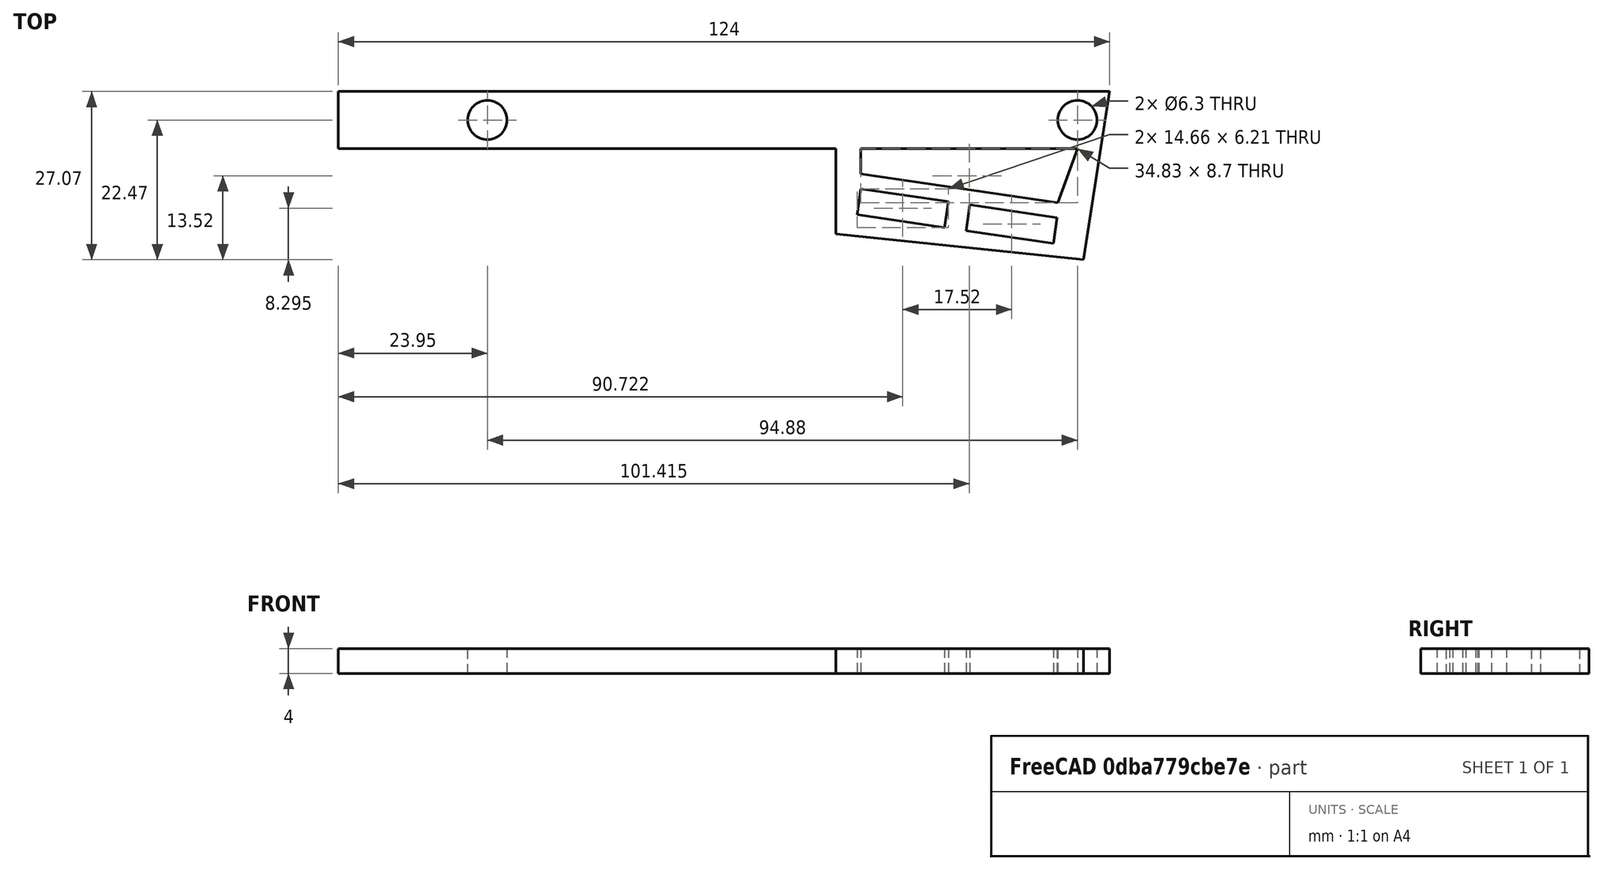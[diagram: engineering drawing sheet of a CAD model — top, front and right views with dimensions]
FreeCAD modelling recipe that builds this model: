
FCSTD DOCUMENT  (FreeCAD 0.18.1R)
Label: CHASSIS
License: All rights reserved
LicenseURL: http://en.wikipedia.org/wiki/All_rights_reserved
objects: TechDraw::DrawViewDimension×12, TechDraw::DrawProjGroupItem×4, Sketcher::SketchObject×2, TechDraw::DrawSVGTemplate×2, TechDraw::DrawPage×2, PartDesign::Pad×1, PartDesign::Plane×1, PartDesign::Pocket×1, PartDesign::Body×1, TechDraw::DrawViewPart×1, TechDraw::DrawProjGroup×1
note: 8 computed .brp shape members not serialized (recipe doc carries the construction recipe); baked Part::Feature solids carry a one-line shape summary decoded from their .brp

FEATURE [Sketcher::SketchObject] Sketch
  MapMode = 5
  Support = -> [XY_Plane]
  sketch-geometry (6):
    g0: LineSegment StartX=0 StartY=9.2 StartZ=0 EndX=0 EndY=0 EndZ=0
    g1: LineSegment StartX=0 StartY=0 StartZ=0 EndX=80 EndY=0 EndZ=0
    g2: LineSegment StartX=80 StartY=0 StartZ=0 EndX=80 EndY=-13.7 EndZ=0
    g3: LineSegment StartX=124 StartY=9.2 StartZ=0 EndX=0 EndY=9.2 EndZ=0
    g4: LineSegment StartX=80 StartY=-13.7 StartZ=0 EndX=119.782 EndY=-17.8733 EndZ=0
    g5: LineSegment StartX=124 StartY=9.2 StartZ=0 EndX=119.782 EndY=-17.8733 EndZ=0
  constraints (17):
    c: Vertical(g0)
    c: Coincident(g0,g1)
    c: Horizontal(g1)
    c: Coincident(g1,g2)
    c: Coincident(g3,g0)
    c: Horizontal(g3)
    c: DistanceX(g3,g3) = 124
    c: DistanceY(g0,g0) = 9.2
    c: DistanceX(g1,g1) = 80
    c: Coincident(g4,g2)
    c: Distance(g4) = 40
    c: Coincident(g5,g3)
    c: Coincident(g5,g4)
    c: Distance(g5) = 27.4
    c: Distance(g2) = 13.7
    c: Vertical(g2)
    c: Coincident(g0,g-1)
FEATURE [PartDesign::Pad] Pad
  Length = 4
  Length2 = 100
  Profile = -> Sketch
  Refine = true
  Type = 0
FEATURE [PartDesign::Plane] DatumPlane
  Length = 146.223
  MapMode = 5
  Placement = pos=(0,0,4) rot=(0,0,1;0rad)
  ResizeMode = 0
  Support = -> [Pad]
  Width = 40.0963
FEATURE [Sketcher::SketchObject] Sketch001
  MapMode = 5
  Placement = pos=(0,0,4) rot=(0,0,1;0rad)
  Support = -> [DatumPlane]
  sketch-geometry (14):
    g0: Circle CenterX=23.95 CenterY=4.6 CenterZ=0 NormalX=0 NormalY=0 NormalZ=1 AngleXU=0 Radius=3.15
    g1: Circle CenterX=118.83 CenterY=4.6 CenterZ=0 NormalX=0 NormalY=0 NormalZ=1 AngleXU=0 Radius=3.15
    g2: LineSegment StartX=84 StartY=0 StartZ=0 EndX=118.83 EndY=0 EndZ=0
    g3: LineSegment StartX=118.83 StartY=0 StartZ=0 EndX=115.67 EndY=-8.7 EndZ=0
    g4: LineSegment StartX=115.67 StartY=-8.7 StartZ=0 EndX=84 EndY=-4.07 EndZ=0
    g5: LineSegment StartX=84 StartY=-4.07 StartZ=0 EndX=84 EndY=0 EndZ=0
    g6: LineSegment StartX=84 StartY=-6.47 StartZ=0 EndX=98.0506 EndY=-8.52414 EndZ=0
    g7: LineSegment StartX=98.0506 StartY=-8.52414 StartZ=0 EndX=97.4431 EndY=-12.68 EndZ=0
    g8: LineSegment StartX=97.4431 StartY=-12.68 StartZ=0 EndX=83.3924 EndY=-10.6258 EndZ=0
    g9: LineSegment StartX=83.3924 StartY=-10.6258 StartZ=0 EndX=84 EndY=-6.47 EndZ=0
    g10: LineSegment StartX=101.52 StartY=-9.03 StartZ=0 EndX=115.571 EndY=-11.0841 EndZ=0
    g11: LineSegment StartX=115.571 StartY=-11.0841 StartZ=0 EndX=114.963 EndY=-15.24 EndZ=0
    g12: LineSegment StartX=114.963 StartY=-15.24 StartZ=0 EndX=100.912 EndY=-13.1858 EndZ=0
    g13: LineSegment StartX=100.912 StartY=-13.1858 StartZ=0 EndX=101.52 EndY=-9.03 EndZ=0
  constraints (42):
    c: Radius(g1) = 3.15
    c: Radius(g0) = 3.15
    c: DistanceX(g-1,g0) = 23.95
    c: DistanceY(g-1,g0) = 4.6
    c: DistanceY(g0,g1) = 0
    c: Horizontal(g2)
    c: Coincident(g2,g3)
    c: Coincident(g3,g4)
    c: Coincident(g4,g5)
    c: Coincident(g5,g2)
    c: DistanceY(g2,g-1) = 0
    c: DistanceX(g-1,g2) = 84
    c: Vertical(g5)
    c: DistanceX(g2,g2) = 34.83
    c: DistanceX(g3,g2) = 3.16
    c: DistanceY(g3,g2) = 8.7
    c: DistanceY(g4,g2) = 4.07
    c: DistanceX(g1,g2) = 0
    c: Coincident(g6,g7)
    c: Coincident(g7,g8)
    c: Coincident(g8,g9)
    c: Coincident(g9,g6)
    c: Coincident(g10,g11)
    c: Coincident(g11,g12)
    c: Coincident(g12,g13)
    c: Coincident(g13,g10)
    c: Parallel(g6,g4)
    c: Parallel(g10,g4)
    c: Distance(g10) = 14.2
    c: Perpendicular(g6,g9)
    c: Perpendicular(g6,g7)
    c: Parallel(g8,g6)
    c: Distance(g7) = 4.2
    c: Perpendicular(g10,g13)
    c: Perpendicular(g10,g11)
    c: Parallel(g12,g10)
    c: Equal(g7,g13)
    c: Equal(g6,g10)
    c: DistanceX(g4,g6) = 0
    c: DistanceY(g6,g4) = 2.4
    c: DistanceY(g10,g4) = 4.96
    c: DistanceX(g4,g10) = 17.52
FEATURE [PartDesign::Pocket] Pocket
  BaseFeature = -> Pad
  Length = 5
  Length2 = 100
  Profile = -> Sketch001
  Refine = true
  Type = 0
FEATURE [PartDesign::Body] Body
  Group = -> [Sketch,Pad,DatumPlane,Sketch001,Pocket]
  Origin = -> Origin
  Tip = -> Pocket
FEATURE [TechDraw::DrawSVGTemplate] Template
  EditableTexts = Designed_by_Name=Designed by Name; Drawing_number=Drawing number; FC-Date=Date; FC-SC=Scale; FC-SH=Sheet; FC-Title=Title; Subtitle=Subtitle; Weight=Weight
  Height = 210
  Orientation = 1
  Width = 297
FEATURE [TechDraw::DrawViewPart] View
  CoarseView = false
  Direction = (0,-1,0)
  Focus = 100
  HardHidden = false
  IsoCount = 0
  IsoHidden = false
  IsoVisible = false
  LockPosition = false
  Perspective = false
  Rotation = 0
  ScaleType = 0
  SeamHidden = false
  SeamVisible = false
  SmoothHidden = false
  SmoothVisible = false
  Source = -> [Body]
  X = 148.5
  Y = 105
FEATURE [TechDraw::DrawPage] Page
  KeepUpdated = true
  ProjectionType = 0
  Template = -> Template
  Views = -> [View]
FEATURE [TechDraw::DrawSVGTemplate] Template001
  EditableTexts = Approved1=Approved 1; Approved2=Approved 2; CheckedBy=Checked By; Code=Code; CompanyAddress=1234 Main St; CompanyName=Company Name; DrawingNumber=Drawing Number; DrawingTitle1=Chassis(RIGHT + LEFT); DrawingTitle2=Drawing Title 2; DrawingTitle3=Drawing Title 3; DrawnBy=Drawn By; Revision=Rev; Scale=Scale; Sheet=Sheet n of m; Weight=Weight
  Height = 279.4
  Orientation = 1
  Width = 431.8
FEATURE [TechDraw::DrawProjGroupItem] ProjItem  label="Front"
  CoarseView = false
  Direction = (0,-1,0)
  Focus = 100
  HardHidden = false
  IsoCount = 0
  IsoHidden = false
  IsoVisible = false
  LockPosition = true
  Perspective = false
  Rotation = 0
  RotationVector = (1,0,0)
  Scale = 2
  ScaleType = 2
  SeamHidden = false
  SeamVisible = false
  SmoothHidden = false
  SmoothVisible = false
  Source = -> [Body]
  Type = 0
  X = 0
  Y = 0
FEATURE [TechDraw::DrawProjGroupItem] ProjItem001  label="Left"
  CoarseView = false
  Direction = (-1,-1e-16,0)
  Focus = 100
  HardHidden = false
  IsoCount = 0
  IsoHidden = false
  IsoVisible = false
  LockPosition = false
  Perspective = false
  Rotation = 0
  RotationVector = (1e-16,-1,0)
  Scale = 2
  ScaleType = 2
  SeamHidden = false
  SeamVisible = false
  SmoothHidden = false
  SmoothVisible = false
  Source = -> [Body]
  Type = 1
  X = 263
  Y = 0
FEATURE [TechDraw::DrawProjGroupItem] ProjItem002  label="FrontTopLeft"
  CoarseView = false
  Direction = (-1,-1,1)
  Focus = 100
  HardHidden = false
  IsoCount = 0
  IsoHidden = false
  IsoVisible = false
  LockPosition = false
  Perspective = false
  Rotation = 0
  RotationVector = (1,-1,0)
  Scale = 2
  ScaleType = 2
  SeamHidden = false
  SeamVisible = false
  SmoothHidden = false
  SmoothVisible = false
  Source = -> [Body]
  Type = 6
  X = 235.939
  Y = -92.3971
FEATURE [TechDraw::DrawProjGroupItem] ProjItem003  label="Top"
  CoarseView = false
  Direction = (0,0,1)
  Focus = 100
  HardHidden = false
  IsoCount = 0
  IsoHidden = false
  IsoVisible = false
  LockPosition = false
  Perspective = false
  Rotation = 0
  RotationVector = (1,0,0)
  Scale = 2
  ScaleType = 2
  SeamHidden = false
  SeamVisible = false
  SmoothHidden = false
  SmoothVisible = false
  Source = -> [Body]
  Type = 4
  X = 0
  Y = -102.398
FEATURE [TechDraw::DrawProjGroup] ProjGroup
  Anchor = -> ProjItem
  AutoDistribute = true
  LockPosition = false
  ProjectionType = 0
  Rotation = 0
  Scale = 2
  ScaleType = 2
  Source = -> [Body]
  Views = -> [ProjItem,ProjItem001,ProjItem002,ProjItem003]
  X = 145.306
  Y = 243.631
  spacingX = 15
  spacingY = 15
FEATURE [TechDraw::DrawViewDimension] Dimension
  Arbitrary = false
  FormatSpec = %.4f
  LockPosition = false
  MeasureType = 1
  OverTolerance = 0
  References2D = -> [ProjItem003]
  Rotation = 0
  ScaleType = 0
  Type = 1
  UnderTolerance = 0
  X = 0
  Y = 41.7805
FEATURE [TechDraw::DrawViewDimension] Dimension001
  Arbitrary = false
  FormatSpec = %.4f
  LockPosition = false
  MeasureType = 1
  OverTolerance = 0
  References2D = -> [ProjItem003]
  Rotation = 0
  ScaleType = 0
  Type = 2
  UnderTolerance = 0
  X = -130.373
  Y = 21.305
FEATURE [TechDraw::DrawViewDimension] Dimension002
  Arbitrary = false
  FormatSpec = %.4f
  LockPosition = false
  MeasureType = 1
  OverTolerance = 0
  References2D = -> [ProjItem003]
  Rotation = 0
  ScaleType = 0
  Type = 1
  UnderTolerance = 0
  X = -44
  Y = 2.79048
FEATURE [TechDraw::DrawViewDimension] Dimension003
  Arbitrary = false
  FormatSpec = %.4f
  LockPosition = false
  MeasureType = 1
  OverTolerance = 0
  References2D = -> [ProjItem003]
  Rotation = 0
  ScaleType = 0
  Type = 2
  UnderTolerance = 0
  X = 12.4686
  Y = -11.3998
FEATURE [TechDraw::DrawViewDimension] Dimension004
  Arbitrary = false
  FormatSpec = %.4f
  LockPosition = false
  MeasureType = 1
  OverTolerance = 0
  References2D = -> [ProjItem003]
  Rotation = 0
  ScaleType = 0
  Type = 1
  UnderTolerance = 0
  X = 78.3398
  Y = 15.0464
FEATURE [TechDraw::DrawViewDimension] Dimension005
  Arbitrary = false
  FormatSpec = ⌀%.4f
  LockPosition = false
  MeasureType = 1
  OverTolerance = 0
  References2D = -> [ProjItem003]
  Rotation = 0
  ScaleType = 0
  Type = 5
  UnderTolerance = 0
  X = 0.490238
  Y = 19.6095
FEATURE [TechDraw::DrawViewDimension] Dimension006
  Arbitrary = false
  FormatSpec = ⌀%.4f
  LockPosition = false
  MeasureType = 1
  OverTolerance = 0
  References2D = -> [ProjItem003]
  Rotation = 0
  ScaleType = 0
  Type = 5
  UnderTolerance = 0
  X = 30.885
  Y = 20.0998
FEATURE [TechDraw::DrawViewDimension] Dimension007
  Arbitrary = false
  FormatSpec = %.4f
  LockPosition = false
  MeasureType = 1
  OverTolerance = 0
  References2D = -> [ProjItem003]
  Rotation = 0
  ScaleType = 0
  Type = 2
  UnderTolerance = 0
  X = 39.0976
  Y = 4.60334
FEATURE [TechDraw::DrawViewDimension] Dimension008
  Arbitrary = false
  FormatSpec = %.4f
  LockPosition = false
  MeasureType = 1
  OverTolerance = 0
  References2D = -> [ProjItem003]
  Rotation = 0
  ScaleType = 0
  Type = 0
  UnderTolerance = 0
  X = 77.1407
  Y = 1.29597
FEATURE [TechDraw::DrawViewDimension] Dimension009
  Arbitrary = false
  FormatSpec = %.4f
  LockPosition = false
  MeasureType = 1
  OverTolerance = 0
  References2D = -> [ProjItem003]
  Rotation = 0
  ScaleType = 0
  Type = 0
  UnderTolerance = 0
  X = 54.1287
  Y = -24.4596
FEATURE [TechDraw::DrawViewDimension] Dimension010
  Arbitrary = false
  FormatSpec = %.4f
  LockPosition = false
  MeasureType = 1
  OverTolerance = 0
  References2D = -> [ProjItem003]
  Rotation = 0
  ScaleType = 0
  Type = 0
  UnderTolerance = 0
  X = 126.155
  Y = -2.45119
FEATURE [TechDraw::DrawViewDimension] Dimension011
  Arbitrary = false
  FormatSpec = %.4f
  LockPosition = false
  MeasureType = 1
  OverTolerance = 0
  References2D = -> [ProjItem003]
  Rotation = 0
  ScaleType = 0
  Type = 0
  UnderTolerance = 0
  X = 108.985
  Y = -17.6508
FEATURE [TechDraw::DrawPage] Page001
  KeepUpdated = true
  ProjectionType = 0
  Template = -> Template001
  Views = -> [ProjGroup,Dimension,Dimension001,Dimension002,Dimension003,Dimension004,Dimension005,Dimension006,Dimension007,Dimension008,Dimension009,Dimension010,Dimension011]
